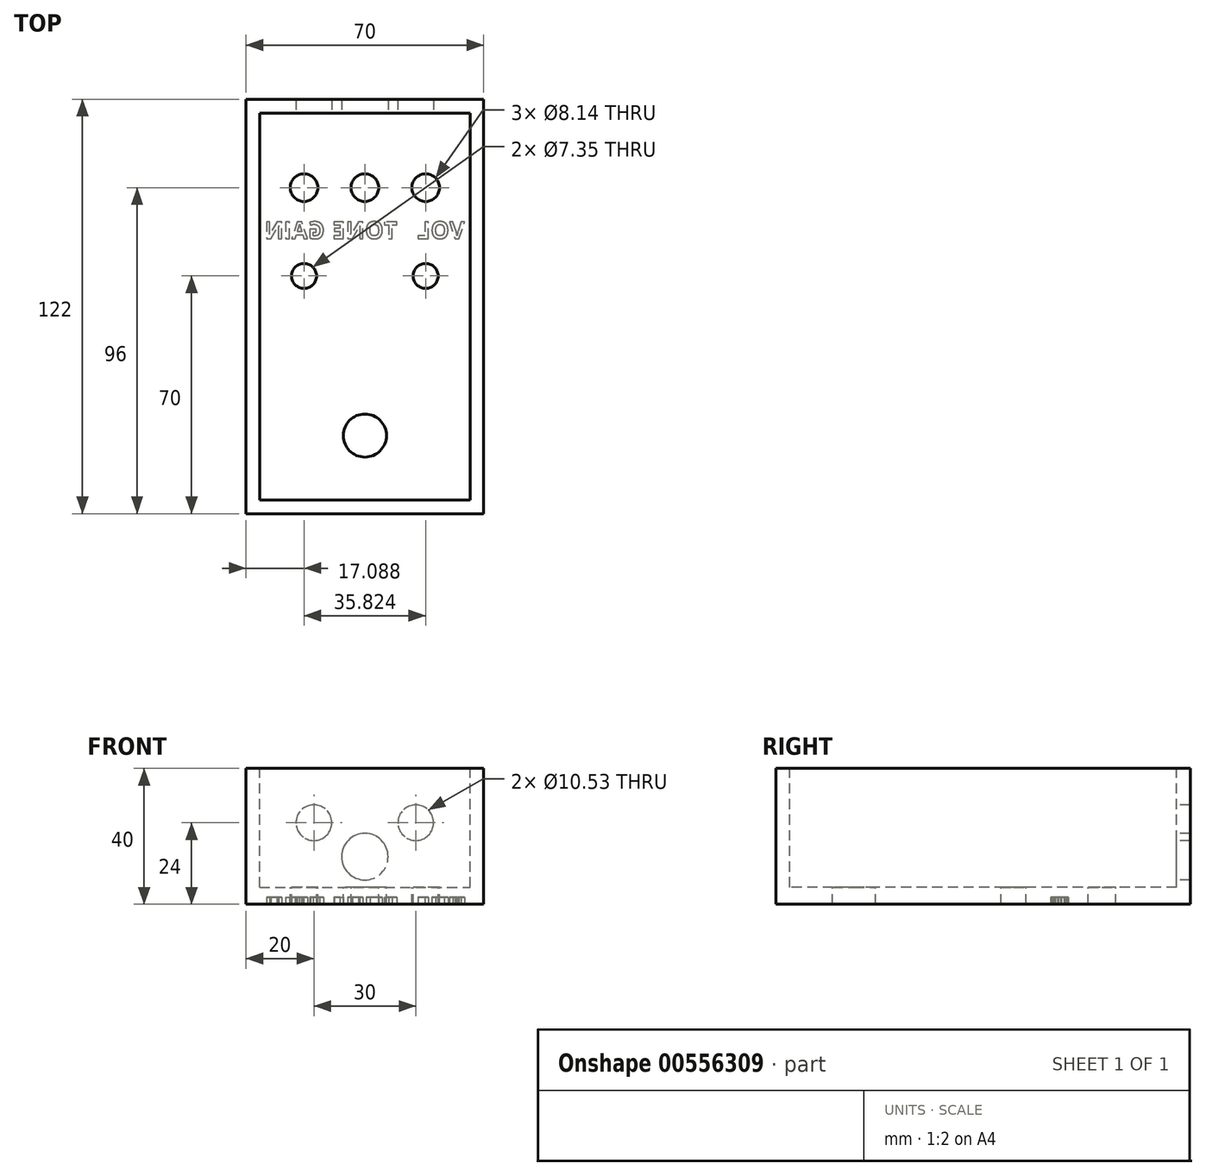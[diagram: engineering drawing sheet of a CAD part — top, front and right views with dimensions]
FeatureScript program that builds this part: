
annotation { "Feature Type Name" : "Feature", "Feature Type Description" : "" }
export const myFeature = defineFeature(function(context is Context, id is Id, definition is map)
    precondition{}
    {
        {
            var Q0;
            Q0=qCreatedBy(makeId("Top.planeOp"),FACE);
            var sketch = newSketch(context, id + "F0", { "sketchPlane" : qUnion([Q0])});
            skLineSegment(sketch, "E0.bottom", {"start": v(-35, 61) * mm, "end": v(35, 61) * mm});
            skLineSegment(sketch, "E0.top", {"start": v(-35, -61) * mm, "end": v(35, -61) * mm});
            skLineSegment(sketch, "E0.left", {"start": v(-35, 61) * mm, "end": v(-35, -61) * mm});
            skLineSegment(sketch, "E0.right", {"start": v(35, 61) * mm, "end": v(35, -61) * mm});
            skSolve(sketch);
        }
        {
            var Q0;
            Q0=makeQuery(id+"F0.imprint","IMPRINT",FACE,{"disambiguationData":[TD([[makeQuery(id+"F0.imprint","IMPRINT",EDGE,{"derivedFrom":sQuery(id+"F0.wireOp",EDGE,"E0.bottom")}),-1.0]])]});
            extrude(context, id + "F1", {"entities" : qUnion([Q0]), "depth" : 40 * mm, "offsetDistance" : 25 * mm});
        }
        {
            var Q0;
            Q0=makeQuery(id+"F1.opExtrude","CAP_FACE",FACE,{"disambiguationData":[OSD([sQuery(id+"F0.wireOp",EDGE,"E0.bottom"),sQuery(id+"F0.wireOp",EDGE,"E0.top"),sQuery(id+"F0.wireOp",EDGE,"E0.left"),sQuery(id+"F0.wireOp",EDGE,"E0.right")])],"isStart":false});
            var sketch = newSketch(context, id + "F2", { "sketchPlane" : qUnion([Q0])});
            skLineSegment(sketch, "E1.bottom", {"start": v(-31, 57) * mm, "end": v(31, 57) * mm});
            skLineSegment(sketch, "E1.top", {"start": v(-31, -57) * mm, "end": v(31, -57) * mm});
            skLineSegment(sketch, "E1.left", {"start": v(-31, 57) * mm, "end": v(-31, -57) * mm});
            skLineSegment(sketch, "E1.right", {"start": v(31, 57) * mm, "end": v(31, -57) * mm});
            skSolve(sketch);
        }
        {
            var Q0;
            Q0=makeQuery(id+"F2.imprint","IMPRINT",FACE,{"disambiguationData":[TD([[makeQuery(id+"F2.imprint","IMPRINT",EDGE,{"derivedFrom":sQuery(id+"F2.wireOp",EDGE,"E1.bottom")}),-1.0]])]});
            extrude(context, id + "F3", {"entities" : qUnion([Q0]), "operationType" : NewBodyOperationType.REMOVE, "oppositeDirection" : true, "depth" : 35 * mm, "offsetDistance" : 25 * mm});
        }
        {
            var Q0;
            Q0=makeQuery(id+"F3.boolean.opBoolean","COPY",FACE,{"derivedFrom":makeQuery(id+"F3.opExtrude","CAP_FACE",FACE,{"disambiguationData":[OSD([sQuery(id+"F2.wireOp",EDGE,"E1.bottom"),sQuery(id+"F2.wireOp",EDGE,"E1.top"),sQuery(id+"F2.wireOp",EDGE,"E1.left"),sQuery(id+"F2.wireOp",EDGE,"E1.right")])],"isStart":false})});
            var sketch = newSketch(context, id + "F4", { "sketchPlane" : qUnion([Q0])});
            skCircle(sketch, "E2", {"center": v(-17.91, 35) * mm, "radius": 4.07 * mm});
            skCircle(sketch, "E3", {"center": v(0, 35) * mm, "radius": 4.07 * mm});
            skCircle(sketch, "E4", {"center": v(17.91, 35) * mm, "radius": 4.07 * mm});
            skCircle(sketch, "E5", {"center": v(17.91, 9) * mm, "radius": 3.67 * mm});
            skCircle(sketch, "E6", {"center": v(0, -38) * mm, "radius": 6.35 * mm});
            skCircle(sketch, "E7", {"center": v(-17.91, 9) * mm, "radius": 3.67 * mm});
            skSolve(sketch);
        }
        {
            var Q0;
            Q0=qSketchRegion(id+"F4",true);
            extrude(context, id + "F5", {"entities" : qUnion([Q0]), "operationType" : NewBodyOperationType.REMOVE, "oppositeDirection" : true, "depth" : 25 * mm, "offsetDistance" : 25 * mm});
        }
        {
            var Q0;
            Q0=makeQuery(id+"F3.boolean.opBoolean","COPY",FACE,{"derivedFrom":makeQuery(id+"F3.opExtrude","SWEPT_FACE",FACE,{"disambiguationData":[OSD([sQuery(id+"F2.wireOp",EDGE,"E1.bottom")])]})});
            var sketch = newSketch(context, id + "F6", { "sketchPlane" : qUnion([Q0])});
            skCircle(sketch, "E8", {"center": v(0, 14) * mm, "radius": 6.85 * mm});
            skCircle(sketch, "E9", {"center": v(15, 24) * mm, "radius": 5.26 * mm});
            skCircle(sketch, "E10", {"center": v(-15, 24) * mm, "radius": 5.26 * mm});
            skSolve(sketch);
        }
        {
            var Q0;
            Q0=qSketchRegion(id+"F6",true);
            extrude(context, id + "F7", {"entities" : qUnion([Q0]), "operationType" : NewBodyOperationType.REMOVE, "oppositeDirection" : true, "depth" : 25 * mm, "offsetDistance" : 25 * mm});
        }
        {
            var Q0;
            Q0=qCreatedBy(makeId("Front.planeOp"),FACE);
            cPlane(context, id + "F8", {"entities" : qUnion([Q0]), "cplaneType" : CPlaneType.OFFSET, "offset" : 38 * mm, "width" : 150 * mm, "height" : 150 * mm});
        }
        {
            var Q0;
            Q0=makeQuery(id+"F1.opExtrude","CAP_FACE",FACE,{"disambiguationData":[OSD([sQuery(id+"F0.wireOp",EDGE,"E0.bottom"),sQuery(id+"F0.wireOp",EDGE,"E0.top"),sQuery(id+"F0.wireOp",EDGE,"E0.left"),sQuery(id+"F0.wireOp",EDGE,"E0.right")])],"isStart":true});
            var sketch = newSketch(context, id + "F9", { "sketchPlane" : qUnion([Q0])});
            skText(sketch, "E11", { "text": "VOL", "fontName": "OpenSans-Bold.ttf"});
            skText(sketch, "E12", { "text": "TONE", "fontName": "OpenSans-Bold.ttf"});
            skText(sketch, "E13", { "text": "GAIN", "fontName": "OpenSans-Bold.ttf"});
            const initialGuessF9  = {"E11": [0.0294, -0.02, -1, 0, 0.005], "E12": [0.00956, -0.02, -1, 0, 0.005], "E13": [-0.0118, -0.02, -1, 0, 0.005]};
            skSetInitialGuess(sketch, initialGuessF9);
            skSolve(sketch);
        }
        {
            var Q0;
            Q0=qSketchRegion(id+"F9",true);
            extrude(context, id + "F10", {"entities" : qUnion([Q0]), "operationType" : NewBodyOperationType.REMOVE, "oppositeDirection" : true, "depth" : 2 * mm, "offsetDistance" : 25 * mm});
        }
    });
